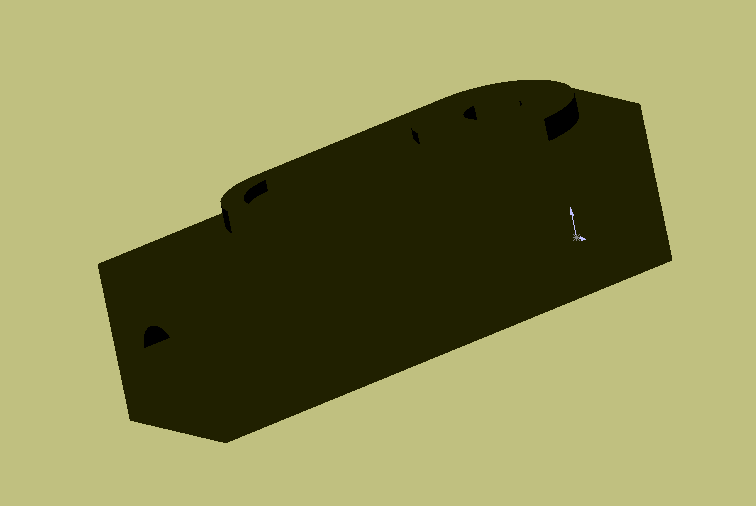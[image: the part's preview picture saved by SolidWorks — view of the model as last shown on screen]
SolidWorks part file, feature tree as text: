
SOLIDWORKS PART (.sldprt)
format: sldprt  version: not decoded by parser v0  size: 121,856 bytes
history: native  units: mm
features: sketch x5, plane x3, cut_extrude x3, extrude x2, material x1 (+8 scaffold rows collapsed)
feature tree (22):
  scaffold x8  (default folders/planes/origin — collapsed)
  material  "Matériau <non spécifié>"
  plane  "Plane1"
  plane  "Plane2"
  plane  "Plane3"
  sketch  "Esquisse1"  dims[D1=7.0mm D2=7.0mm]
  extrude  "Base-Extrusion"  Depth=23.5mm
  sketch  "Esquisse2"  dims[c1.D3=7.0mm c1.D1=5.0mm c1.D2=3.5mm c1.D4=10.0mm c2.D2=7.0mm c2.D3=3.5mm]
  extrude  "Boss.-Extru.1"  Depth=1mm
  sketch  "Esquisse3"  dims[D1=2.5mm]
  cut_extrude  "Enlèv. mat.-Extru.1"  [1 undecoded]
  sketch  "Esquisse4"  dims[D1=5.0mm]
  cut_extrude  "Enlèv. mat.-Extru.2"  Depth=0.5mm
  sketch  "Esquisse5"  dims[D1=2.5mm]
  cut_extrude  "Enlèv. mat.-Extru.3"  Depth=10mm
decode coverage: 9 of 10 modeling features carry decoded parameters
note: 1 parameter value undecoded
note: suppression state not decoded; provenance and decode notes live in map.json
